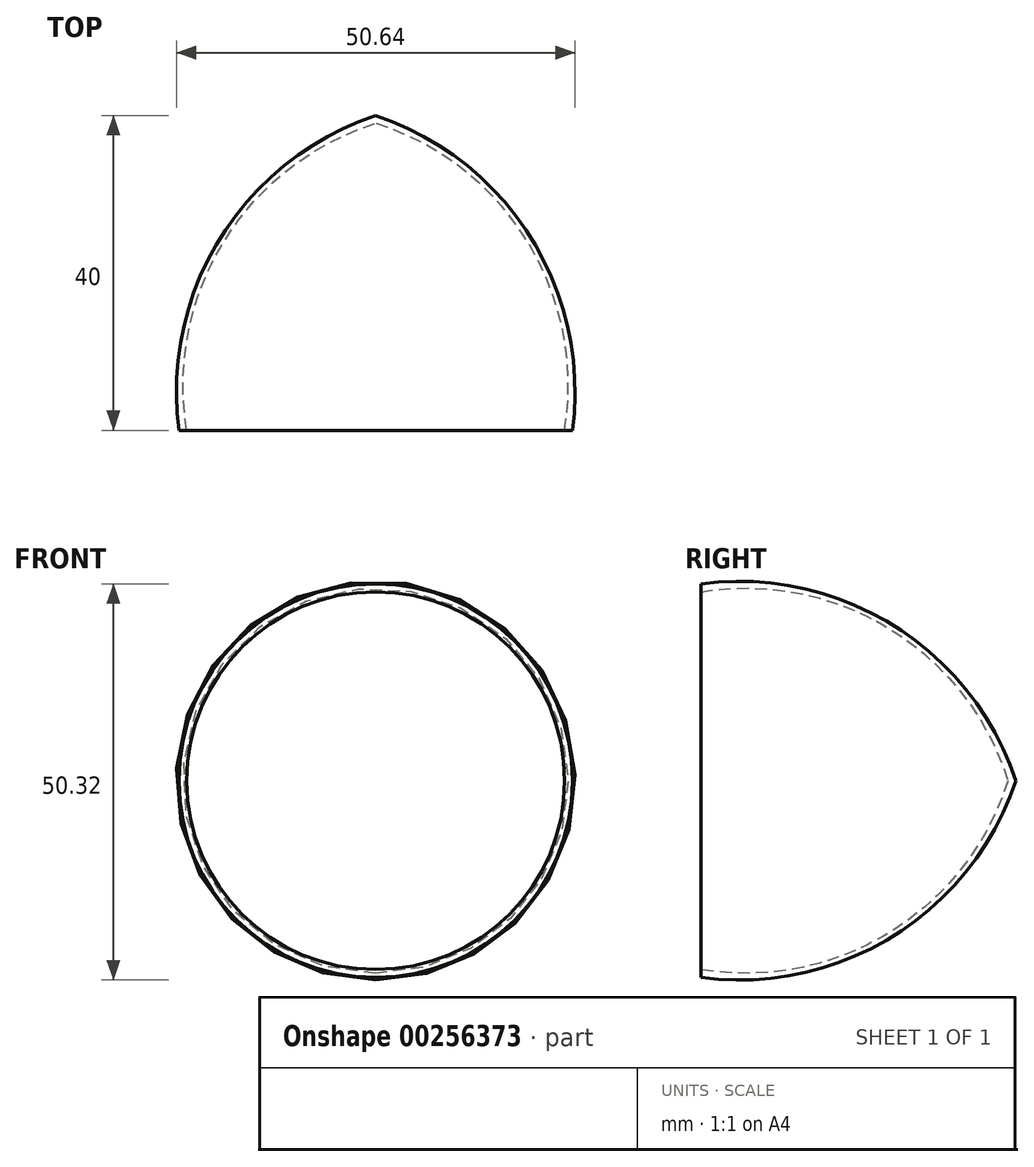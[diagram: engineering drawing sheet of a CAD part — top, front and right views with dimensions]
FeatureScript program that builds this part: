
annotation { "Feature Type Name" : "Feature", "Feature Type Description" : "" }
export const myFeature = defineFeature(function(context is Context, id is Id, definition is map)
    precondition{}
    {
        {
            var Q0;
            Q0=qCreatedBy(makeId("Top.planeOp"),FACE);
            var sketch = newSketch(context, id + "F0", { "sketchPlane" : qUnion([Q0])});
            skLineSegment(sketch, "E0", {"start": v(-25, 0) * mm, "end": v(-24, 0) * mm});
            skLineSegment(sketch, "E1", {"start": v(0, -20) * mm, "end": v(0, -19) * mm});
            skLineSegment(sketch, "E2", {"start": v(0, 40) * mm, "end": v(0, 39) * mm});
            skArc(sketch, "E3", {"start": v(-24, 0) * mm, "mid": v(0, -19) * mm, "end": v(24, 0) * mm});
            skArc(sketch, "E4", {"start": v(-25, 0) * mm, "mid": v(0, -20) * mm, "end": v(25, 0) * mm});
            skArc(sketch, "E5", {"start": v(0, 39) * mm, "mid": v(-19.29, 23.98) * mm, "end": v(-24, 0) * mm});
            skArc(sketch, "E6", {"start": v(24, 0) * mm, "mid": v(19.29, 23.98) * mm, "end": v(0, 39) * mm});
            skArc(sketch, "E7", {"start": v(0, 40) * mm, "mid": v(-19.7, 24.5) * mm, "end": v(-25, 0) * mm});
            skArc(sketch, "E8", {"start": v(25, 0) * mm, "mid": v(19.7, 24.5) * mm, "end": v(0, 40) * mm});
            skLineSegment(sketch, "E9", {"start": v(0, 39) * mm, "end": v(0, 0) * mm});
            skLineSegment(sketch, "E10", {"start": v(25, 0) * mm, "end": v(24, 0) * mm});
            skLineSegment(sketch, "E11", {"start": v(-24, 0) * mm, "end": v(24, 0) * mm});
            skLineSegment(sketch, "E12", {"start": v(-11.7, 0) * mm, "end": v(-24, 0) * mm});
            skLineSegment(sketch, "E13", {"start": v(-10.44, 0) * mm, "end": v(-11.7, 0) * mm});
            skSolve(sketch);
        }
        {
            var Q0;
            Q0=makeQuery(id+"F0.imprint","IMPRINT",FACE,{"disambiguationData":[TD([[makeQuery(id+"F0.imprint","IMPRINT",EDGE,{"derivedFrom":sQuery(id+"F0.wireOp",EDGE,"E0")}),1.0]])]});
            var Q1;
            {var subQ0=sQuery(id+"F0.wireOp",EDGE,"dX1uFb2T-ENYY-vfWl-Eug2-N4xyPCVQ4jqE");var subQ3=sQuery(id+"F0.wireOp",EDGE,"PHVocTqT-oGUS-vaHj-E7xn-t1QSrxUSIeDI");var subQ5=makeQuery(id+"F0.imprint","INTERSECT",VERTEX,{"derivedFrom":[subQ3,subQ0]});Q1=makeQuery(id+"F0.imprint","IMPRINT",FACE,{"disambiguationData":[TD([[makeQuery(id+"F0.imprint","IMPRINT",EDGE,{"disambiguationData":[TD([[subQ5,1.0]])],"derivedFrom":subQ3}),-1.0]])]});}
            var Q2;
            Q2=sQuery(id+"F0.wireOp",EDGE,"E9");
            revolve(context, id + "F1", {"entities" : qUnion([Q0, Q1]), "axis" : qUnion([Q2]), "revolveType" : RevolveType.SYMMETRIC, "angle" : 360 * degree});
        }
    });
